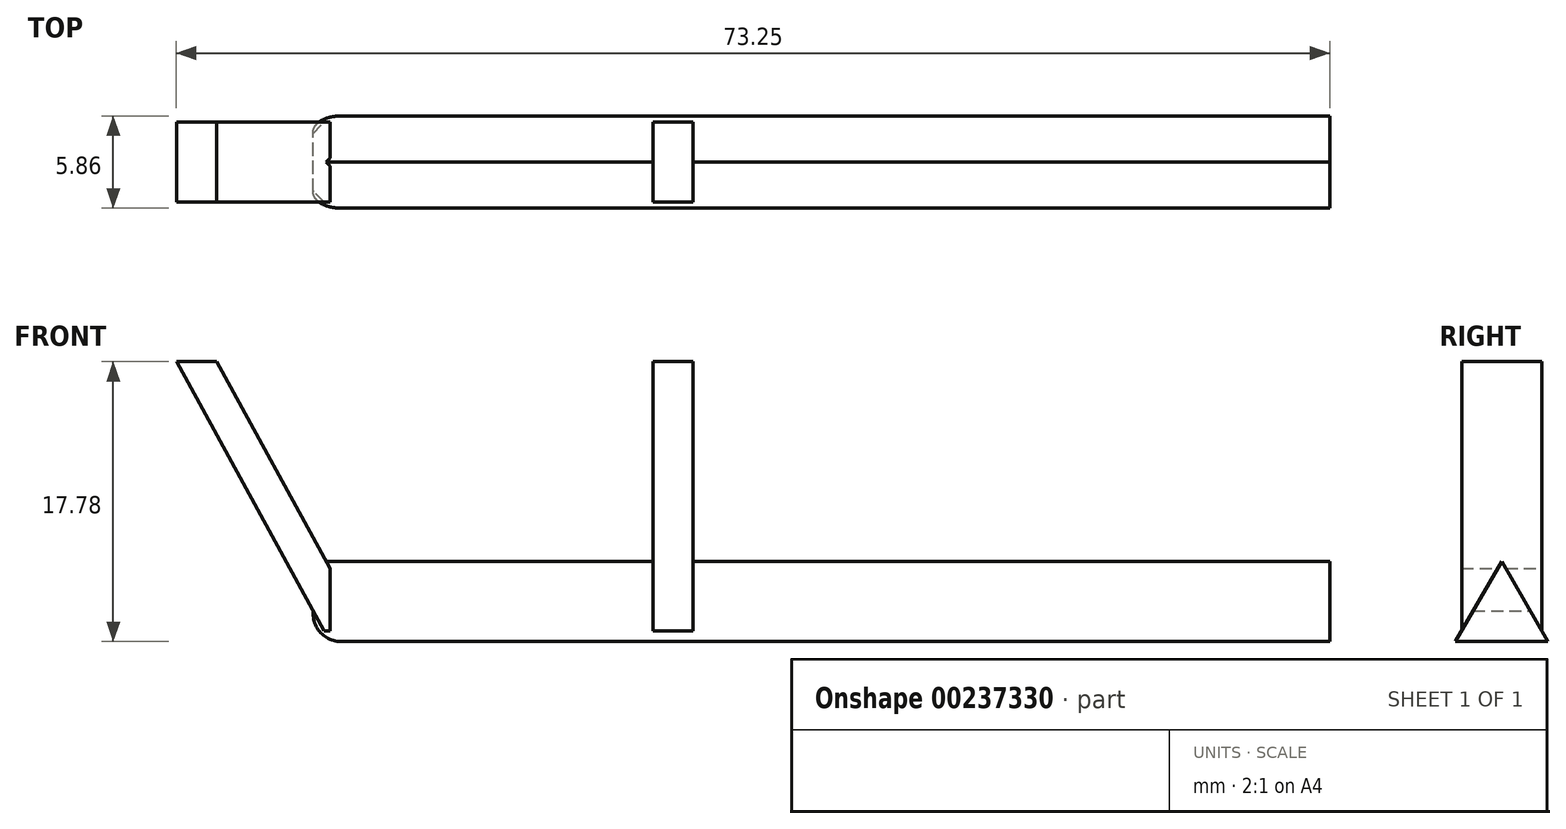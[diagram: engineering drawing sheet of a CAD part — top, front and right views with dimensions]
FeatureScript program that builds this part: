
annotation { "Feature Type Name" : "Feature", "Feature Type Description" : "" }
export const myFeature = defineFeature(function(context is Context, id is Id, definition is map)
    precondition{}
    {
        {
            var Q0;
            Q0=qCreatedBy(makeId("Right.planeOp"),FACE);
            var sketch = newSketch(context, id + "F0", { "sketchPlane" : qUnion([Q0])});
            skLineSegment(sketch, "E0", {"start": v(0, 5.08) * mm, "end": v(-2.93, 0) * mm});
            skLineSegment(sketch, "E1", {"start": v(-2.93, 0) * mm, "end": v(2.93, 0) * mm});
            skLineSegment(sketch, "E2", {"start": v(2.93, 0) * mm, "end": v(0, 5.08) * mm});
            skSolve(sketch);
        }
        {
            var Q0;
            Q0=makeQuery(id+"F0.imprint","IMPRINT",FACE,{"disambiguationData":[TD([[makeQuery(id+"F0.imprint","IMPRINT",EDGE,{"derivedFrom":sQuery(id+"F0.wireOp",EDGE,"E0")}),1.0]])]});
            extrude(context, id + "F1", {"entities" : qUnion([Q0]), "offsetDistance" : 25.4 * mm, "depth" : 63.5 * mm, "hasSecondDirection" : true, "secondDirectionOppositeDirection" : true, "secondDirectionDepth" : 1.07 * mm});
        }
        {
            var Q0;
            Q0=qCreatedBy(makeId("Front.planeOp"),FACE);
            var sketch = newSketch(context, id + "F2", { "sketchPlane" : qUnion([Q0])});
            skLineSegment(sketch, "E3", {"start": v(20.51, 0) * mm, "end": v(20.51, 17.78) * mm});
            skLineSegment(sketch, "E4", {"start": v(20.51, 17.78) * mm, "end": v(23.05, 17.78) * mm});
            skLineSegment(sketch, "E5", {"start": v(23.05, 17.78) * mm, "end": v(23.05, 0) * mm});
            skLineSegment(sketch, "E6", {"start": v(23.05, 0) * mm, "end": v(20.51, 0) * mm});
            skLineSegment(sketch, "E7", {"start": v(0, 0) * mm, "end": v(-9.75, 17.78) * mm});
            skLineSegment(sketch, "E8", {"start": v(-9.75, 17.78) * mm, "end": v(-7.2, 17.78) * mm});
            skLineSegment(sketch, "E9", {"start": v(-7.2, 17.78) * mm, "end": v(0, 4.63) * mm});
            skLineSegment(sketch, "E10", {"start": v(0, 4.63) * mm, "end": v(0, 0) * mm});
            skSolve(sketch);
        }
        {
            var Q0;
            Q0=makeQuery(id+"F2.imprint","IMPRINT",FACE,{"disambiguationData":[TD([[makeQuery(id+"F2.imprint","IMPRINT",EDGE,{"derivedFrom":sQuery(id+"F2.wireOp",EDGE,"3GbCVj1j-LeCn-g0jc-bS3x-EMcVDivOLz6L")}),-1.0]])]});
            var Q1;
            Q1=makeQuery(id+"F2.imprint","IMPRINT",FACE,{"disambiguationData":[TD([[makeQuery(id+"F2.imprint","IMPRINT",EDGE,{"derivedFrom":sQuery(id+"F2.wireOp",EDGE,"E3")}),-1.0]])]});
            extrude(context, id + "F3", {"entities" : qUnion([Q0, Q1]), "operationType" : NewBodyOperationType.ADD, "offsetDistance" : 25.4 * mm, "depth" : 5.08 * mm, "symmetric" : true});
        }
        {
            var Q0;
            Q0=makeQuery(id+"F2.imprint","IMPRINT",FACE,{"disambiguationData":[TD([[makeQuery(id+"F2.imprint","IMPRINT",EDGE,{"derivedFrom":sQuery(id+"F2.wireOp",EDGE,"E7")}),-1.0]])]});
            extrude(context, id + "F4", {"entities" : qUnion([Q0]), "operationType" : NewBodyOperationType.ADD, "offsetDistance" : 25.4 * mm, "depth" : 5.08 * mm, "symmetric" : true});
        }
        {
            var Q0;
            Q0=makeQuery(id+"F1.opExtrude","CAP_EDGE",EDGE,{"disambiguationData":[OSD([sQuery(id+"F0.wireOp",EDGE,"E1")])],"isStart":true});
            fillet(context, id + "F5", {"entities" : qUnion([Q0]), "tangentPropagation" : true, "radius" : 1.78 * mm, "defaultsChanged" : true, "vertexSettings" : [], "allowEdgeOverflow" : false});
        }
    });
